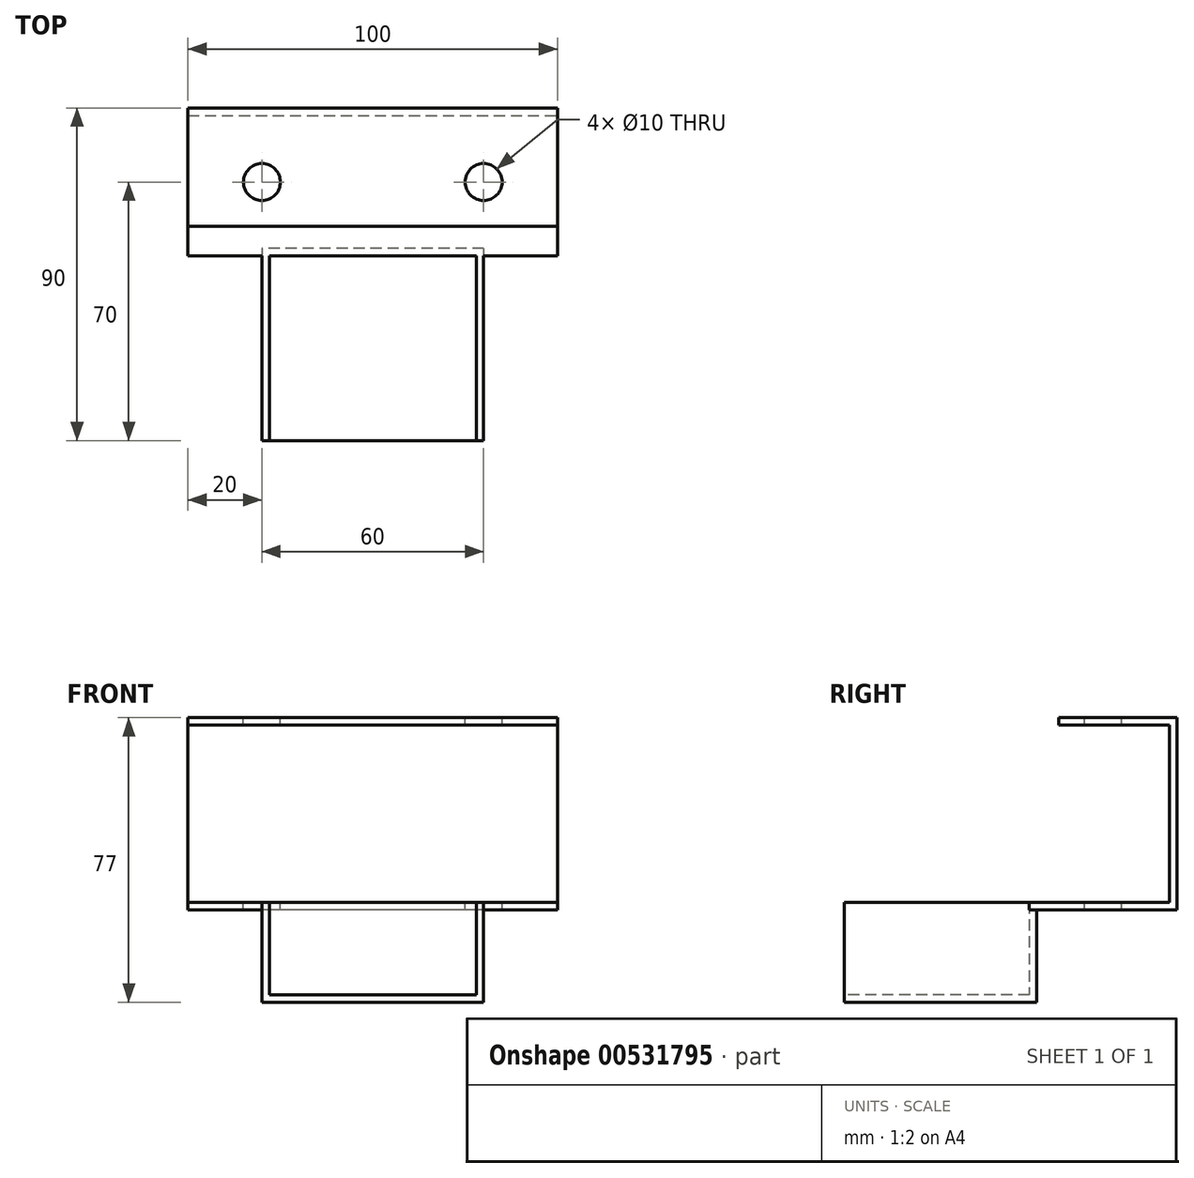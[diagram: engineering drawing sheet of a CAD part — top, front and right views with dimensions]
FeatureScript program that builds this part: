
annotation { "Feature Type Name" : "Feature", "Feature Type Description" : "" }
export const myFeature = defineFeature(function(context is Context, id is Id, definition is map)
    precondition{}
    {
        {
            var Q0;
            Q0=qCreatedBy(makeId("Top.planeOp"),FACE);
            var sketch = newSketch(context, id + "F0", { "sketchPlane" : qUnion([Q0])});
            skLineSegment(sketch, "E0.bottom", {"start": v(50, 20) * mm, "end": v(-50, 20) * mm});
            skLineSegment(sketch, "E0.top", {"start": v(50, -20) * mm, "end": v(-50, -20) * mm});
            skLineSegment(sketch, "E0.left", {"start": v(50, 20) * mm, "end": v(50, -20) * mm});
            skLineSegment(sketch, "E0.right", {"start": v(-50, 20) * mm, "end": v(-50, -20) * mm});
            skPoint(sketch, "E0.middle", {"position": v(0, 0) * mm});
            skSolve(sketch);
        }
        {
            var Q0;
            Q0=makeQuery(id+"F0.imprint","IMPRINT",FACE,{"disambiguationData":[TD([[makeQuery(id+"F0.imprint","IMPRINT",EDGE,{"derivedFrom":sQuery(id+"F0.wireOp",EDGE,"E0.bottom")}),1.0]])]});
            extrude(context, id + "F1", {"entities" : qUnion([Q0]), "depth" : 2 * mm, "offsetDistance" : 25 * mm});
        }
        {
            var Q0;
            Q0=makeQuery(id+"F1.opExtrude","CAP_FACE",FACE,{"disambiguationData":[OSD([sQuery(id+"F0.wireOp",EDGE,"E0.bottom"),sQuery(id+"F0.wireOp",EDGE,"E0.top"),sQuery(id+"F0.wireOp",EDGE,"E0.left"),sQuery(id+"F0.wireOp",EDGE,"E0.right")])],"isStart":false});
            var sketch = newSketch(context, id + "F2", { "sketchPlane" : qUnion([Q0])});
            skLineSegment(sketch, "E1.bottom", {"start": v(-50, 20) * mm, "end": v(50, 20) * mm});
            skLineSegment(sketch, "E1.top", {"start": v(-50, 18) * mm, "end": v(50, 18) * mm});
            skLineSegment(sketch, "E1.left", {"start": v(-50, 20) * mm, "end": v(-50, 18) * mm});
            skLineSegment(sketch, "E1.right", {"start": v(50, 20) * mm, "end": v(50, 18) * mm});
            skSolve(sketch);
        }
        {
            var Q0;
            Q0=makeQuery(id+"F2.imprint","IMPRINT",FACE,{"disambiguationData":[TD([[makeQuery(id+"F2.imprint","IMPRINT",EDGE,{"derivedFrom":sQuery(id+"F2.wireOp",EDGE,"E1.bottom")}),1.0]])]});
            extrude(context, id + "F3", {"entities" : qUnion([Q0]), "operationType" : NewBodyOperationType.ADD, "depth" : 50 * mm, "offsetDistance" : 25 * mm});
        }
        {
            var Q0;
            Q0=makeQuery(id+"F3.opExtrude","SWEPT_FACE",FACE,{"disambiguationData":[OSD([sQuery(id+"F2.wireOp",EDGE,"E1.top")])]});
            var sketch = newSketch(context, id + "F4", { "sketchPlane" : qUnion([Q0])});
            skLineSegment(sketch, "E2.bottom", {"start": v(-50, 52) * mm, "end": v(50, 52) * mm});
            skLineSegment(sketch, "E2.top", {"start": v(-50, 50) * mm, "end": v(50, 50) * mm});
            skLineSegment(sketch, "E2.left", {"start": v(-50, 52) * mm, "end": v(-50, 50) * mm});
            skLineSegment(sketch, "E2.right", {"start": v(50, 52) * mm, "end": v(50, 50) * mm});
            skSolve(sketch);
        }
        {
            var Q0;
            Q0 = qSketchRegion(id + "F4", true);
            extrude(context, id + "F5", {"entities" : qUnion([Q0]), "operationType" : NewBodyOperationType.ADD, "depth" : 30 * mm, "offsetDistance" : 25 * mm});
        }
        {
            var Q0;
            Q0=makeQuery(id+"F5.boolean.opBoolean","MERGE",FACE,{"derivedFrom":[makeQuery(id+"F3.opExtrude","CAP_FACE",FACE,{"disambiguationData":[OSD([sQuery(id+"F2.wireOp",EDGE,"E1.bottom"),sQuery(id+"F2.wireOp",EDGE,"E1.top"),sQuery(id+"F2.wireOp",EDGE,"E1.left"),sQuery(id+"F2.wireOp",EDGE,"E1.right")])],"isStart":false}),makeQuery(id+"F5.opExtrude","SWEPT_FACE",FACE,{"disambiguationData":[OSD([sQuery(id+"F4.wireOp",EDGE,"E2.bottom")])]})]});
            var sketch = newSketch(context, id + "F6", { "sketchPlane" : qUnion([Q0])});
            skLineSegment(sketch, "E3.left", {"start": v(30, 0) * mm, "end": v(30, 0) * mm});
            skLineSegment(sketch, "E3.right", {"start": v(-30, 0) * mm, "end": v(-30, 0) * mm});
            skPoint(sketch, "E3.middle", {"position": v(0, 0) * mm});
            skCircle(sketch, "E4", {"center": v(30, 0) * mm, "radius": 5 * mm});
            skCircle(sketch, "E5", {"center": v(-30, 0) * mm, "radius": 5 * mm});
            skSolve(sketch);
        }
        {
            var Q0;
            Q0 = qSketchRegion(id + "F6", true);
            extrude(context, id + "F7", {"entities" : qUnion([Q0]), "operationType" : NewBodyOperationType.REMOVE, "oppositeDirection" : true, "depth" : 100 * mm, "offsetDistance" : 25 * mm});
        }
        {
            var Q0;
            Q0=makeQuery(id+"F1.opExtrude","CAP_FACE",FACE,{"disambiguationData":[OSD([sQuery(id+"F0.wireOp",EDGE,"E0.bottom"),sQuery(id+"F0.wireOp",EDGE,"E0.top"),sQuery(id+"F0.wireOp",EDGE,"E0.left"),sQuery(id+"F0.wireOp",EDGE,"E0.right")])],"isStart":true});
            var sketch = newSketch(context, id + "F8", { "sketchPlane" : qUnion([Q0])});
            skPoint(sketch, "E6.endSnap0", {"position": v(0, 20) * mm});
            skLineSegment(sketch, "E7.bottom", {"start": v(30, 18) * mm, "end": v(-30, 18) * mm});
            skLineSegment(sketch, "E7.top", {"start": v(30, 20) * mm, "end": v(-30, 20) * mm});
            skLineSegment(sketch, "E7.left", {"start": v(30, 18) * mm, "end": v(30, 20) * mm});
            skLineSegment(sketch, "E7.right", {"start": v(-30, 18) * mm, "end": v(-30, 20) * mm});
            skPoint(sketch, "E7.middle", {"position": v(0, 19) * mm});
            skPoint(sketch, "E6.start.orphan", {"position": v(0, 20) * mm});
            skSolve(sketch);
        }
        {
            var Q0;
            Q0 = qSketchRegion(id + "F8", true);
            extrude(context, id + "F9", {"entities" : qUnion([Q0]), "operationType" : NewBodyOperationType.ADD, "depth" : 25 * mm, "offsetDistance" : 25 * mm});
        }
        {
            var Q0;
            Q0=makeQuery(id+"F9.boolean.opBoolean","MERGE",FACE,{"derivedFrom":[makeQuery(id+"F1.opExtrude","SWEPT_FACE",FACE,{"disambiguationData":[OSD([sQuery(id+"F0.wireOp",EDGE,"E0.top")])]}),makeQuery(id+"F9.opExtrude","SWEPT_FACE",FACE,{"disambiguationData":[OSD([sQuery(id+"F8.wireOp",EDGE,"E7.top")])]})]});
            var sketch = newSketch(context, id + "F10", { "sketchPlane" : qUnion([Q0])});
            skLineSegment(sketch, "E8.bottom", {"start": v(-30, -25) * mm, "end": v(30, -25) * mm});
            skLineSegment(sketch, "E8.top", {"start": v(-30, -23) * mm, "end": v(30, -23) * mm});
            skLineSegment(sketch, "E8.left", {"start": v(-30, -25) * mm, "end": v(-30, -23) * mm});
            skLineSegment(sketch, "E8.right", {"start": v(30, -25) * mm, "end": v(30, -23) * mm});
            skSolve(sketch);
        }
        {
            var Q0;
            Q0 = qSketchRegion(id + "F10", true);
            extrude(context, id + "F11", {"entities" : qUnion([Q0]), "operationType" : NewBodyOperationType.ADD, "depth" : 50 * mm, "offsetDistance" : 25 * mm});
        }
        {
            var Q0;
            Q0=makeQuery(id+"F11.opExtrude","SWEPT_FACE",FACE,{"disambiguationData":[OSD([sQuery(id+"F10.wireOp",EDGE,"E8.top")])]});
            var sketch = newSketch(context, id + "F12", { "sketchPlane" : qUnion([Q0])});
            skLineSegment(sketch, "E9.bottom", {"start": v(-30, -20) * mm, "end": v(-28, -20) * mm});
            skLineSegment(sketch, "E9.top", {"start": v(-30, -70) * mm, "end": v(-28, -70) * mm});
            skLineSegment(sketch, "E9.left", {"start": v(-30, -20) * mm, "end": v(-30, -70) * mm});
            skLineSegment(sketch, "E9.right", {"start": v(-28, -20) * mm, "end": v(-28, -70) * mm});
            skLineSegment(sketch, "E10.bottom", {"start": v(30, -20) * mm, "end": v(28, -20) * mm});
            skLineSegment(sketch, "E10.top", {"start": v(30, -70) * mm, "end": v(28, -70) * mm});
            skLineSegment(sketch, "E10.left", {"start": v(30, -20) * mm, "end": v(30, -70) * mm});
            skLineSegment(sketch, "E10.right", {"start": v(28, -20) * mm, "end": v(28, -70) * mm});
            skSolve(sketch);
        }
        {
            var Q0;
            Q0 = qSketchRegion(id + "F12", true);
            extrude(context, id + "F13", {"entities" : qUnion([Q0]), "operationType" : NewBodyOperationType.ADD, "depth" : 25 * mm, "offsetDistance" : 25 * mm});
        }
    });
